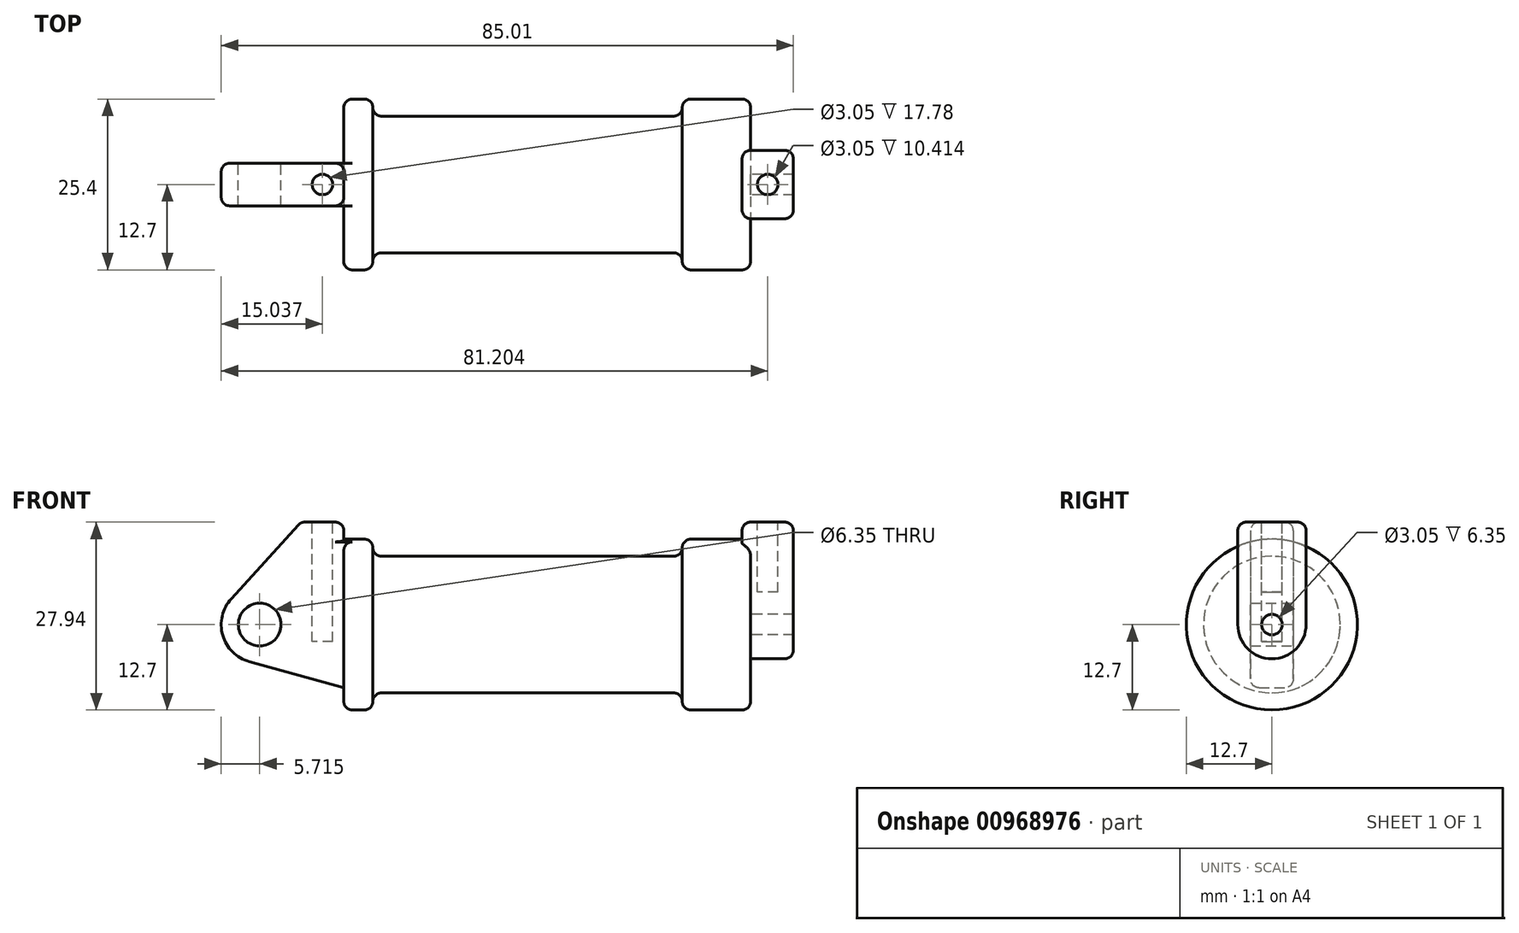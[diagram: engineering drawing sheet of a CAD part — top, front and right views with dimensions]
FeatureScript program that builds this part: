
annotation { "Feature Type Name" : "Feature", "Feature Type Description" : "" }
export const myFeature = defineFeature(function(context is Context, id is Id, definition is map)
    precondition{}
    {
        {
            var Q0;
            Q0=qCreatedBy(makeId("Front.planeOp"),FACE);
            var sketch = newSketch(context, id + "F0", { "sketchPlane" : qUnion([Q0])});
            skLineSegment(sketch, "E0", {"start": v(0, 0) * mm, "end": v(0, 12.7) * mm});
            skLineSegment(sketch, "E1", {"start": v(0, 12.7) * mm, "end": v(10.16, 12.7) * mm});
            skLineSegment(sketch, "E2", {"start": v(10.16, 12.7) * mm, "end": v(10.16, 10.16) * mm});
            skLineSegment(sketch, "E3", {"start": v(10.16, 10.16) * mm, "end": v(56.13, 10.16) * mm});
            skLineSegment(sketch, "E4", {"start": v(56.13, 10.16) * mm, "end": v(56.13, 12.7) * mm});
            skLineSegment(sketch, "E5", {"start": v(56.13, 12.7) * mm, "end": v(66.3, 12.7) * mm});
            skLineSegment(sketch, "E6", {"start": v(66.3, 12.7) * mm, "end": v(66.3, 0) * mm});
            skLineSegment(sketch, "E7", {"start": v(66.3, 0) * mm, "end": v(0, 0) * mm});
            skLineSegment(sketch, "E8", {"start": v(5.84, 15.24) * mm, "end": v(-0.5, 15.24) * mm});
            skLineSegment(sketch, "E9", {"start": v(-0.5, 15.24) * mm, "end": v(-10.88, 3.85) * mm});
            skLineSegment(sketch, "E10", {"start": v(0, 0) * mm, "end": v(-6.65, 0) * mm});
            skCircle(sketch, "E11", {"center": v(-6.65, 0) * mm, "radius": 5.72 * mm});
            skCircle(sketch, "E12", {"center": v(-6.65, 0) * mm, "radius": 3.18 * mm});
            skLineSegment(sketch, "E13", {"start": v(5.84, 15.24) * mm, "end": v(5.84, -9.4) * mm});
            skLineSegment(sketch, "E14", {"start": v(5.84, -9.4) * mm, "end": v(-8.18, -5.5) * mm});
            skSolve(sketch);
        }
        {
            var Q0;
            {var subQ0=sQuery(id+"F0.wireOp",EDGE,"E2");Q0=makeQuery(id+"F0.imprint","IMPRINT",FACE,{"disambiguationData":[TD([[makeQuery(id+"F0.imprint","IMPRINT",EDGE,{"derivedFrom":subQ0}),-1.0]])]});}
            var Q1;
            Q1=sQuery(id+"F0.wireOp",EDGE,"E7");
            revolve(context, id + "F1", {"surfaceOperationType" : NewSurfaceOperationType.NEW, "entities" : qUnion([Q0]), "axis" : qUnion([Q1]), "revolveType" : RevolveType.FULL});
        }
        {
            var Q0;
            {var subQ1=sQuery(id+"F0.wireOp",EDGE,"E0");Q0=makeQuery(id+"F0.imprint","IMPRINT",FACE,{"disambiguationData":[TD([[makeQuery(id+"F0.imprint","IMPRINT",EDGE,{"derivedFrom":subQ1}),1.0]])]});}
            var Q1;
            {var subQ0=sQuery(id+"F0.wireOp",EDGE,"E0");Q1=makeQuery(id+"F0.imprint","IMPRINT",FACE,{"disambiguationData":[TD([[makeQuery(id+"F0.imprint","IMPRINT",EDGE,{"derivedFrom":subQ0}),-1.0]])]});}
            var Q2;
            {var subQ5=sQuery(id+"F0.wireOp",EDGE,"E12");Q2=makeQuery(id+"F0.imprint","IMPRINT",FACE,{"disambiguationData":[TD([[makeQuery(id+"F0.imprint","IMPRINT",EDGE,{"derivedFrom":subQ5}),-1.0]])]});}
            var Q3;
            {var subQ0=sQuery(id+"F0.wireOp",EDGE,"E14");Q3=makeQuery(id+"F0.imprint","IMPRINT",FACE,{"disambiguationData":[TD([[makeQuery(id+"F0.imprint","IMPRINT",EDGE,{"derivedFrom":subQ0}),-1.0]])]});}
            extrude(context, id + "F2", {"entities" : qUnion([Q0, Q1, Q2, Q3]), "operationType" : NewBodyOperationType.ADD, "endBound" : BoundingType.SYMMETRIC, "depth" : 6.35 * mm, "offsetDistance" : 25.4 * mm});
        }
        {
            var Q0;
            Q0=makeQuery(id+"F1.opRevolve","SWEPT_FACE",FACE,{"disambiguationData":[OSD([sQuery(id+"F0.wireOp",EDGE,"E6")])]});
            var sketch = newSketch(context, id + "F3", { "sketchPlane" : qUnion([Q0])});
            skCircle(sketch, "E15", {"center": v(0, 0) * mm, "radius": 1.52 * mm});
            skCircle(sketch, "E16", {"center": v(0, 0) * mm, "radius": 5.08 * mm});
            skLineSegment(sketch, "E17", {"start": v(0, 0) * mm, "end": v(-5.08, 0) * mm, "construction": true});
            skLineSegment(sketch, "E18", {"start": v(-5.08, 0) * mm, "end": v(5.08, 0) * mm, "construction": true});
            skLineSegment(sketch, "E19", {"start": v(-5.08, 0) * mm, "end": v(-5.08, 15.24) * mm});
            skLineSegment(sketch, "E20", {"start": v(5.08, 0) * mm, "end": v(5.08, 15.24) * mm});
            skLineSegment(sketch, "E21", {"start": v(-5.08, 15.24) * mm, "end": v(5.08, 15.24) * mm});
            skSolve(sketch);
        }
        {
            var Q0;
            Q0 = qSketchRegion(id + "F3", true);
            extrude(context, id + "F4", {"entities" : qUnion([Q0]), "operationType" : NewBodyOperationType.ADD, "oppositeDirection" : true, "depth" : 1.27 * mm, "offsetDistance" : 25.4 * mm});
        }
        {
            var Q0;
            {var subQ0=sQuery(id+"F3.wireOp",EDGE,"E21");Q0=makeQuery(id+"F3.imprint","IMPRINT",FACE,{"disambiguationData":[TD([[makeQuery(id+"F3.imprint","IMPRINT",EDGE,{"derivedFrom":subQ0}),-1.0]])]});}
            var Q1;
            {var subQ0=sQuery(id+"F3.wireOp",EDGE,"E19");var subQ1=sQuery(id+"F3.wireOp",EDGE,"E16");var subQ2=makeQuery(id+"F3.imprint","INTERSECT",VERTEX,{"derivedFrom":[subQ1,subQ0]});Q1=makeQuery(id+"F3.imprint","IMPRINT",FACE,{"disambiguationData":[TD([[makeQuery(id+"F3.imprint","IMPRINT",EDGE,{"disambiguationData":[TD([[subQ2,1.0]])],"derivedFrom":subQ1}),-1.0]])]});}
            var Q2;
            Q2=makeQuery(id+"F3.imprint","IMPRINT",FACE,{"disambiguationData":[TD([[makeQuery(id+"F3.imprint","IMPRINT",EDGE,{"derivedFrom":sQuery(id+"F3.wireOp",EDGE,"E15")}),-1.0]])]});
            extrude(context, id + "F5", {"entities" : qUnion([Q0, Q1, Q2]), "operationType" : NewBodyOperationType.ADD, "depth" : 6.35 * mm, "offsetDistance" : 25.4 * mm});
        }
        {
            var Q0;
            Q0=makeQuery(id+"F2.opExtrude","SWEPT_FACE",FACE,{"disambiguationData":[OSD([sQuery(id+"F0.wireOp",EDGE,"E8")])]});
            var sketch = newSketch(context, id + "F6", { "sketchPlane" : qUnion([Q0])});
            skLineSegment(sketch, "E22", {"start": v(2.67, 3.18) * mm, "end": v(2.67, -3.18) * mm, "construction": true});
            skLineSegment(sketch, "E23", {"start": v(5.84, 0) * mm, "end": v(-0.5, 0) * mm, "construction": true});
            skCircle(sketch, "E24", {"center": v(2.67, 0) * mm, "radius": 1.52 * mm});
            skSolve(sketch);
        }
        {
            var Q0;
            Q0=makeQuery(id+"F6.imprint","IMPRINT",FACE,{"disambiguationData":[TD([[makeQuery(id+"F6.imprint","IMPRINT",EDGE,{"derivedFrom":sQuery(id+"F6.wireOp",EDGE,"E24")}),1.0]])]});
            extrude(context, id + "F7", {"entities" : qUnion([Q0]), "operationType" : NewBodyOperationType.REMOVE, "oppositeDirection" : true, "depth" : 17.78 * mm, "offsetDistance" : 25.4 * mm});
        }
        {
            var Q0;
            {var subQ0=sQuery(id+"F3.wireOp",EDGE,"E21");Q0=makeQuery(id+"F5.boolean.opBoolean","MERGE",FACE,{"derivedFrom":[makeQuery(id+"F4.opExtrude","SWEPT_FACE",FACE,{"disambiguationData":[OSD([subQ0])]}),makeQuery(id+"F5.opExtrude","SWEPT_FACE",FACE,{"disambiguationData":[OSD([subQ0])]})]});}
            var sketch = newSketch(context, id + "F8", { "sketchPlane" : qUnion([Q0])});
            skLineSegment(sketch, "E25", {"start": v(68.83, 5.08) * mm, "end": v(68.83, -5.08) * mm, "construction": true});
            skLineSegment(sketch, "E26", {"start": v(65.02, 0) * mm, "end": v(72.64, 0) * mm, "construction": true});
            skCircle(sketch, "E27", {"center": v(68.83, 0) * mm, "radius": 1.52 * mm});
            skSolve(sketch);
        }
        {
            var Q0;
            Q0=makeQuery(id+"F8.imprint","IMPRINT",FACE,{"disambiguationData":[TD([[makeQuery(id+"F8.imprint","IMPRINT",EDGE,{"derivedFrom":sQuery(id+"F8.wireOp",EDGE,"E27")}),1.0]])]});
            var Q1;
            Q1=sQuery(id+"F8.wireOp",EDGE,"E27");
            extrude(context, id + "F9", {"entities" : qUnion([Q0]), "operationType" : NewBodyOperationType.REMOVE, "surfaceEntities" : qUnion([Q1]), "oppositeDirection" : true, "depth" : 10.4 * mm, "offsetDistance" : 25.4 * mm});
        }
        {
            var Q0;
            Q0=makeQuery(id+"F1.opRevolve","SWEPT_EDGE",EDGE,{"disambiguationData":[OSD([sQuery(id+"F0.wireOp",EDGE,"E2"),sQuery(id+"F0.wireOp",EDGE,"E3")])]});
            var Q1;
            Q1=makeQuery(id+"F1.opRevolve","SWEPT_EDGE",EDGE,{"disambiguationData":[OSD([sQuery(id+"F0.wireOp",EDGE,"E1"),sQuery(id+"F0.wireOp",EDGE,"E2")])]});
            var Q2;
            Q2=makeQuery(id+"F1.opRevolve","SWEPT_EDGE",EDGE,{"disambiguationData":[OSD([sQuery(id+"F0.wireOp",EDGE,"E4"),sQuery(id+"F0.wireOp",EDGE,"E5")])]});
            var Q3;
            Q3=makeQuery(id+"F1.opRevolve","SWEPT_EDGE",EDGE,{"disambiguationData":[OSD([sQuery(id+"F0.wireOp",EDGE,"E3"),sQuery(id+"F0.wireOp",EDGE,"E4")])]});
            var Q4;
            {var subQ0=sQuery(id+"F0.wireOp",EDGE,"E1");var subQ1=sQuery(id+"F0.wireOp",EDGE,"E13");Q4=makeQuery(id+"F2.boolean.opBoolean","SPLIT",EDGE,{"disambiguationData":[topologyDisambiguationEdgeConnected([makeQuery(id+"F1.opRevolve","SWEPT_FACE",FACE,{"disambiguationData":[OSD([subQ1])]})])],"derivedFrom":makeQuery(id+"F1.opRevolve","SWEPT_EDGE",EDGE,{"disambiguationData":[OSD([subQ0,subQ1])]})});}
            var Q5;
            Q5=makeQuery(id+"F1.opRevolve","SWEPT_EDGE",EDGE,{"disambiguationData":[OSD([sQuery(id+"F0.wireOp",EDGE,"E5"),sQuery(id+"F0.wireOp",EDGE,"E6")])]});
            fillet(context, id + "F10", {"entities" : qUnion([Q0, Q1, Q2, Q3, Q4, Q5]), "radius" : 1.27 * mm, "tangentPropagation" : true, "allowEdgeOverflow" : false});
        }
        {
            var Q0;
            Q0=makeQuery(id+"F2.opExtrude","CAP_EDGE",EDGE,{"disambiguationData":[OSD([sQuery(id+"F0.wireOp",EDGE,"E8")])],"isStart":true});
            var Q1;
            Q1=makeQuery(id+"F2.opExtrude","SWEPT_EDGE",EDGE,{"disambiguationData":[OSD([sQuery(id+"F0.wireOp",EDGE,"E8"),sQuery(id+"F0.wireOp",EDGE,"E9")])]});
            var Q2;
            Q2=makeQuery(id+"F2.opExtrude","CAP_EDGE",EDGE,{"disambiguationData":[OSD([sQuery(id+"F0.wireOp",EDGE,"E8")])],"isStart":false});
            var Q3;
            Q3=makeQuery(id+"F2.opExtrude","SWEPT_EDGE",EDGE,{"disambiguationData":[OSD([sQuery(id+"F0.wireOp",EDGE,"E8"),sQuery(id+"F0.wireOp",EDGE,"E13")])]});
            var Q4;
            {var subQ0=sQuery(id+"F0.wireOp",EDGE,"E13");Q4=makeQuery(id+"F10.opFillet","TWEAK_EDGE",EDGE,{"derivedFrom":[makeQuery(id+"F2.boolean.opBoolean","TWEAK_VERTEX",VERTEX,{"derivedFrom":[makeQuery(id+"F1.opRevolve","SWEPT_FACE",FACE,{"disambiguationData":[OSD([sQuery(id+"F0.wireOp",EDGE,"E1")])]}),makeQuery(id+"F1.opRevolve","SWEPT_FACE",FACE,{"disambiguationData":[OSD([subQ0])]}),makeQuery(id+"F2.opExtrude","CAP_FACE",FACE,{"disambiguationData":[OSD([sQuery(id+"F0.wireOp",EDGE,"E8"),sQuery(id+"F0.wireOp",EDGE,"E9"),sQuery(id+"F0.wireOp",EDGE,"E11"),sQuery(id+"F0.wireOp",EDGE,"E12"),subQ0,sQuery(id+"F0.wireOp",EDGE,"E14")])],"isStart":true}),makeQuery(id+"F2.opExtrude","SWEPT_FACE",FACE,{"disambiguationData":[OSD([subQ0])]})]})]});}
            var Q5;
            {var subQ0=sQuery(id+"F0.wireOp",EDGE,"E13");Q5=makeQuery(id+"F2.boolean.opBoolean","SPLIT",EDGE,{"disambiguationData":[topologyDisambiguationEdgeConnected([makeQuery(id+"F2.opExtrude","SWEPT_FACE",FACE,{"disambiguationData":[OSD([subQ0])]})])],"derivedFrom":makeQuery(id+"F2.opExtrude","CAP_EDGE",EDGE,{"disambiguationData":[OSD([subQ0])],"isStart":true})});}
            var Q6;
            {var subQ0=sQuery(id+"F0.wireOp",EDGE,"E13");Q6=makeQuery(id+"F2.boolean.opBoolean","SPLIT",EDGE,{"disambiguationData":[topologyDisambiguationEdgeConnected([makeQuery(id+"F2.opExtrude","SWEPT_FACE",FACE,{"disambiguationData":[OSD([subQ0])]})])],"derivedFrom":makeQuery(id+"F2.opExtrude","CAP_EDGE",EDGE,{"disambiguationData":[OSD([subQ0])],"isStart":false})});}
            var Q7;
            Q7=makeQuery(id+"F2.opExtrude","CAP_EDGE",EDGE,{"disambiguationData":[OSD([sQuery(id+"F0.wireOp",EDGE,"E9")])],"isStart":true});
            var Q8;
            Q8=makeQuery(id+"F2.opExtrude","CAP_EDGE",EDGE,{"disambiguationData":[OSD([sQuery(id+"F0.wireOp",EDGE,"E9")])],"isStart":false});
            var Q9;
            {var subQ0=sQuery(id+"F0.wireOp",EDGE,"E13");Q9=makeQuery(id+"F10.opFillet","TWEAK_EDGE",EDGE,{"derivedFrom":[makeQuery(id+"F2.boolean.opBoolean","TWEAK_VERTEX",VERTEX,{"derivedFrom":[makeQuery(id+"F1.opRevolve","SWEPT_FACE",FACE,{"disambiguationData":[OSD([sQuery(id+"F0.wireOp",EDGE,"E1")])]}),makeQuery(id+"F1.opRevolve","SWEPT_FACE",FACE,{"disambiguationData":[OSD([subQ0])]}),makeQuery(id+"F2.opExtrude","CAP_FACE",FACE,{"disambiguationData":[OSD([sQuery(id+"F0.wireOp",EDGE,"E8"),sQuery(id+"F0.wireOp",EDGE,"E9"),sQuery(id+"F0.wireOp",EDGE,"E11"),sQuery(id+"F0.wireOp",EDGE,"E12"),subQ0,sQuery(id+"F0.wireOp",EDGE,"E14")])],"isStart":false}),makeQuery(id+"F2.opExtrude","SWEPT_FACE",FACE,{"disambiguationData":[OSD([subQ0])]})]})]});}
            fillet(context, id + "F11", {"entities" : qUnion([Q0, Q1, Q2, Q3, Q4, Q5, Q6, Q7, Q8, Q9]), "radius" : 1.27 * mm, "tangentPropagation" : true, "allowEdgeOverflow" : false});
        }
        {
            var Q0;
            Q0=makeQuery(id+"F4.opExtrude","CAP_EDGE",EDGE,{"disambiguationData":[OSD([sQuery(id+"F3.wireOp",EDGE,"E19")])],"isStart":false});
            var Q1;
            {var subQ0=sQuery(id+"F3.wireOp",EDGE,"E21");var subQ1=sQuery(id+"F3.wireOp",EDGE,"E19");Q1=makeQuery(id+"F5.boolean.opBoolean","MERGE",EDGE,{"derivedFrom":[makeQuery(id+"F4.opExtrude","SWEPT_EDGE",EDGE,{"disambiguationData":[OSD([subQ1,subQ0])]}),makeQuery(id+"F5.opExtrude","SWEPT_EDGE",EDGE,{"disambiguationData":[OSD([subQ1,subQ0])]})]});}
            var Q2;
            Q2=makeQuery(id+"F5.opExtrude","CAP_EDGE",EDGE,{"disambiguationData":[OSD([sQuery(id+"F3.wireOp",EDGE,"E19")])],"isStart":false});
            var Q3;
            {var subQ0=sQuery(id+"F3.wireOp",EDGE,"E21");var subQ1=sQuery(id+"F3.wireOp",EDGE,"E20");Q3=makeQuery(id+"F5.boolean.opBoolean","MERGE",EDGE,{"derivedFrom":[makeQuery(id+"F4.opExtrude","SWEPT_EDGE",EDGE,{"disambiguationData":[OSD([subQ1,subQ0])]}),makeQuery(id+"F5.opExtrude","SWEPT_EDGE",EDGE,{"disambiguationData":[OSD([subQ1,subQ0])]})]});}
            var Q4;
            Q4=makeQuery(id+"F4.opExtrude","CAP_EDGE",EDGE,{"disambiguationData":[OSD([sQuery(id+"F3.wireOp",EDGE,"E21")])],"isStart":false});
            var Q5;
            Q5=makeQuery(id+"F5.opExtrude","CAP_EDGE",EDGE,{"disambiguationData":[OSD([sQuery(id+"F3.wireOp",EDGE,"E21")])],"isStart":false});
            var Q6;
            Q6=makeQuery(id+"F4.opExtrude","CAP_EDGE",EDGE,{"disambiguationData":[OSD([sQuery(id+"F3.wireOp",EDGE,"E20")])],"isStart":false});
            fillet(context, id + "F12", {"entities" : qUnion([Q0, Q1, Q2, Q3, Q4, Q5, Q6]), "radius" : 1.27 * mm, "tangentPropagation" : true, "allowEdgeOverflow" : false});
        }
    });
